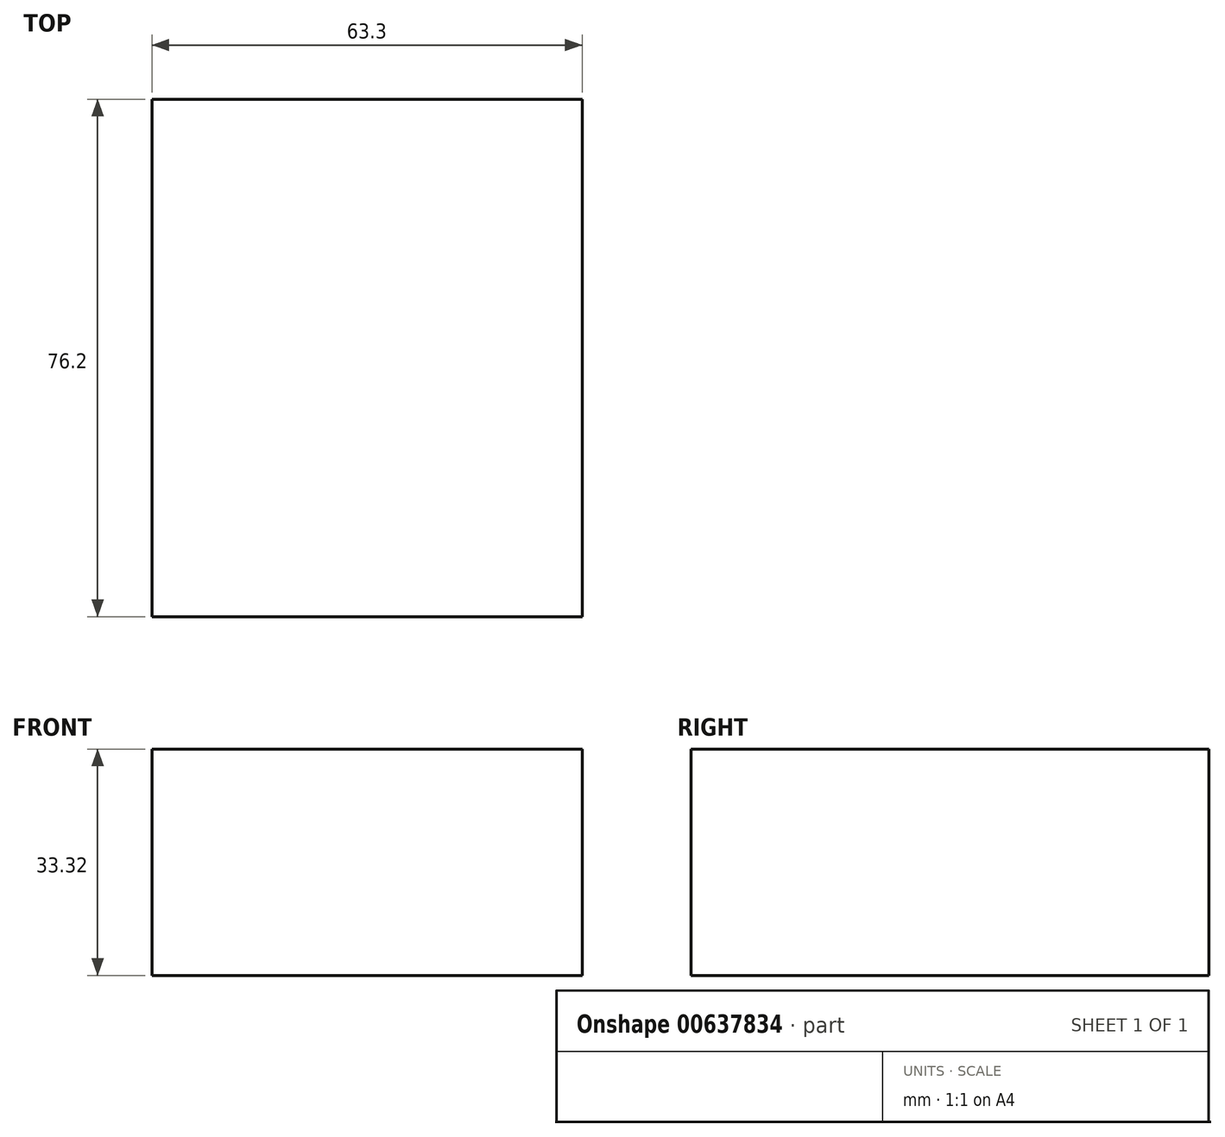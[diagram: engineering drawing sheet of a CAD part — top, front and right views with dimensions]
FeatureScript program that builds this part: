
annotation { "Feature Type Name" : "Feature", "Feature Type Description" : "" }
export const myFeature = defineFeature(function(context is Context, id is Id, definition is map)
    precondition{}
    {
        {
            var Q0;
            Q0=qCreatedBy(makeId("Front.planeOp"),FACE);
            var sketch = newSketch(context, id + "F0", { "sketchPlane" : qUnion([Q0])});
            skLineSegment(sketch, "E0.bottom", {"start": v(0, 0) * mm, "end": v(-63.3, 0) * mm});
            skLineSegment(sketch, "E0.top", {"start": v(0, 33.32) * mm, "end": v(-63.3, 33.32) * mm});
            skLineSegment(sketch, "E0.left", {"start": v(0, 0) * mm, "end": v(0, 33.32) * mm});
            skLineSegment(sketch, "E0.right", {"start": v(-63.3, 0) * mm, "end": v(-63.3, 33.32) * mm});
            skSolve(sketch);
        }
        {
            var Q0;
            Q0=makeQuery(id+"F0.imprint","IMPRINT",FACE,{"disambiguationData":[TD([[makeQuery(id+"F0.imprint","IMPRINT",EDGE,{"derivedFrom":sQuery(id+"F0.wireOp",EDGE,"E0.bottom")}),-1.0]])]});
            extrude(context, id + "F1", {"entities" : qUnion([Q0]), "depth" : 76.2 * mm, "offsetDistance" : 25.4 * mm});
        }
    });
